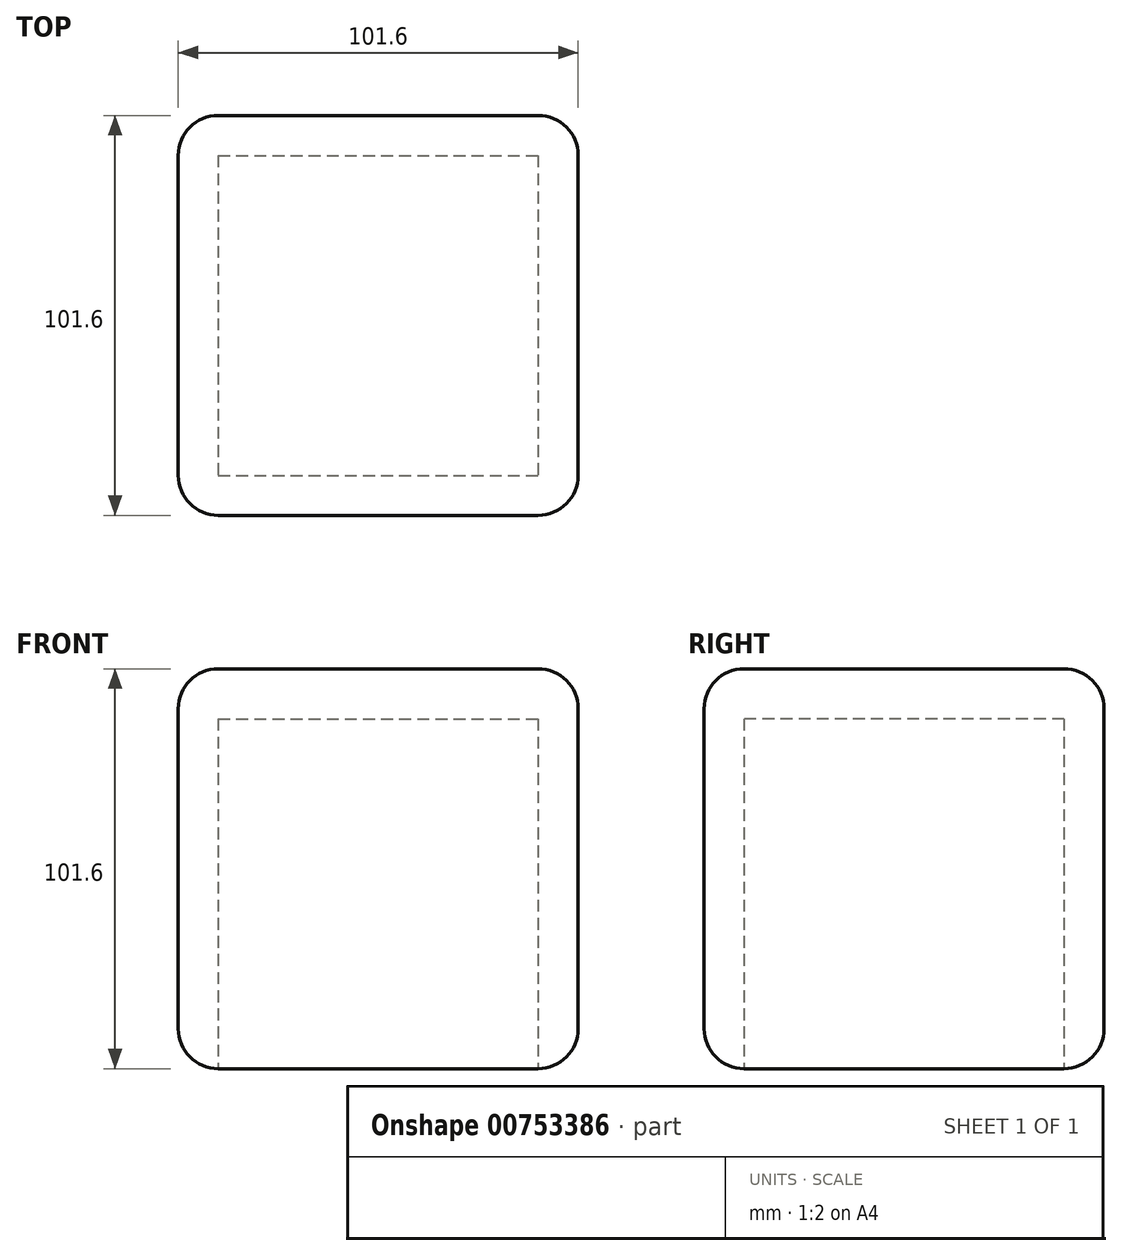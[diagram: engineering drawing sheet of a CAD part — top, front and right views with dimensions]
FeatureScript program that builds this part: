
annotation { "Feature Type Name" : "Feature", "Feature Type Description" : "" }
export const myFeature = defineFeature(function(context is Context, id is Id, definition is map)
    precondition{}
    {
        {
            var Q0;
            Q0=qCreatedBy(makeId("Top.planeOp"),FACE);
            var sketch = newSketch(context, id + "F0", { "sketchPlane" : qUnion([Q0])});
            skLineSegment(sketch, "E0.bottom", {"start": v(-50.8, 50.8) * mm, "end": v(50.8, 50.8) * mm});
            skLineSegment(sketch, "E0.top", {"start": v(-50.8, -50.8) * mm, "end": v(50.8, -50.8) * mm});
            skLineSegment(sketch, "E0.left", {"start": v(-50.8, 50.8) * mm, "end": v(-50.8, -50.8) * mm});
            skLineSegment(sketch, "E0.right", {"start": v(50.8, 50.8) * mm, "end": v(50.8, -50.8) * mm});
            skPoint(sketch, "E0.middle", {"position": v(0, 0) * mm});
            skSolve(sketch);
        }
        {
            var Q0;
            Q0=makeQuery(id+"F0.imprint","IMPRINT",FACE,{"disambiguationData":[TD([[makeQuery(id+"F0.imprint","IMPRINT",EDGE,{"derivedFrom":sQuery(id+"F0.wireOp",EDGE,"E0.bottom")}),-1.0]])]});
            extrude(context, id + "F1", {"entities" : qUnion([Q0]), "depth" : 101.6 * mm, "offsetDistance" : 25.4 * mm});
        }
        {
            var Q0;
            Q0=qCreatedBy(makeId("Top.planeOp"),FACE);
            var sketch = newSketch(context, id + "F2", { "sketchPlane" : qUnion([Q0])});
            skCircle(sketch, "E1", {"center": v(0, 0) * mm, "radius": 50.8 * mm});
            skSolve(sketch);
        }
        {
            var Q0;
            Q0=makeQuery(id+"F2.imprint","IMPRINT",FACE,{"disambiguationData":[TD([[makeQuery(id+"F2.imprint","IMPRINT",EDGE,{"derivedFrom":sQuery(id+"F2.wireOp",EDGE,"E1")}),1.0]])]});
            extrude(context, id + "F3", {"entities" : qUnion([Q0]), "depth" : 101.6 * mm, "offsetDistance" : 25.4 * mm});
        }
        {
            var Q0;
            Q0=qCreatedBy(makeId("Front.planeOp"),FACE);
            var sketch = newSketch(context, id + "F4", { "sketchPlane" : qUnion([Q0])});
            skArc(sketch, "E2", {"start": v(42.89, -27.22) * mm, "mid": v(27.22, 42.89) * mm, "end": v(-42.89, 27.22) * mm});
            skLineSegment(sketch, "E3", {"start": v(-42.89, 27.22) * mm, "end": v(42.89, -27.22) * mm});
            skSolve(sketch);
        }
        {
            var Q0;
            Q0=makeQuery(id+"F4.imprint","IMPRINT",FACE,{"disambiguationData":[TD([[makeQuery(id+"F4.imprint","IMPRINT",EDGE,{"derivedFrom":sQuery(id+"F4.wireOp",EDGE,"E2")}),1.0]])]});
            var Q1;
            Q1=sQuery(id+"F4.wireOp",EDGE,"E3");
            revolve(context, id + "F5", {"surfaceOperationType" : NewSurfaceOperationType.NEW, "entities" : qUnion([Q0]), "axis" : qUnion([Q1]), "revolveType" : RevolveType.FULL});
        }
        {
            var Q0;
            Q0=makeQuery(id+"F1.opExtrude","SWEPT_BODY",BODY,{"disambiguationData":[OSD([sQuery(id+"F0.wireOp",EDGE,"E0.bottom"),sQuery(id+"F0.wireOp",EDGE,"E0.top"),sQuery(id+"F0.wireOp",EDGE,"E0.left"),sQuery(id+"F0.wireOp",EDGE,"E0.right")])]});
            deleteBodies(context, id + "F6", {"entities" : qUnion([Q0])});
        }
        {
            var Q0;
            Q0=makeQuery(id+"F3.opExtrude","SWEPT_BODY",BODY,{"disambiguationData":[OSD([sQuery(id+"F2.wireOp",EDGE,"E1")])]});
            deleteBodies(context, id + "F7", {"entities" : qUnion([Q0])});
        }
        {
            var Q0;
            Q0=makeQuery(id+"F5.opRevolve","SWEPT_BODY",BODY,{"disambiguationData":[OSD([sQuery(id+"F4.wireOp",EDGE,"E2"),sQuery(id+"F4.wireOp",EDGE,"E3")])]});
            deleteBodies(context, id + "F8", {"entities" : qUnion([Q0])});
        }
        {
            var Q0;
            Q0=qCreatedBy(makeId("Top.planeOp"),FACE);
            var sketch = newSketch(context, id + "F9", { "sketchPlane" : qUnion([Q0])});
            skLineSegment(sketch, "E4.bottom", {"start": v(-50.8, 50.8) * mm, "end": v(50.8, 50.8) * mm});
            skLineSegment(sketch, "E4.top", {"start": v(-50.8, -50.8) * mm, "end": v(50.8, -50.8) * mm});
            skLineSegment(sketch, "E4.left", {"start": v(-50.8, 50.8) * mm, "end": v(-50.8, -50.8) * mm});
            skLineSegment(sketch, "E4.right", {"start": v(50.8, 50.8) * mm, "end": v(50.8, -50.8) * mm});
            skPoint(sketch, "E4.middle", {"position": v(0, 0) * mm});
            skSolve(sketch);
        }
        {
            var Q0;
            Q0 = qSketchRegion(id + "F9", true);
            extrude(context, id + "F10", {"entities" : qUnion([Q0]), "depth" : 101.6 * mm, "offsetDistance" : 25.4 * mm});
        }
        {
            var Q0;
            Q0=makeQuery(id+"F10.opExtrude","SWEPT_EDGE",EDGE,{"disambiguationData":[OSD([sQuery(id+"F9.wireOp",EDGE,"E4.bottom"),sQuery(id+"F9.wireOp",EDGE,"E4.left")])]});
            var Q1;
            Q1=makeQuery(id+"F10.opExtrude","CAP_EDGE",EDGE,{"disambiguationData":[OSD([sQuery(id+"F9.wireOp",EDGE,"E4.left")])],"isStart":false});
            var Q2;
            Q2=makeQuery(id+"F10.opExtrude","CAP_EDGE",EDGE,{"disambiguationData":[OSD([sQuery(id+"F9.wireOp",EDGE,"E4.bottom")])],"isStart":false});
            var Q3;
            Q3=makeQuery(id+"F10.opExtrude","CAP_EDGE",EDGE,{"disambiguationData":[OSD([sQuery(id+"F9.wireOp",EDGE,"E4.right")])],"isStart":false});
            var Q4;
            Q4=makeQuery(id+"F10.opExtrude","SWEPT_EDGE",EDGE,{"disambiguationData":[OSD([sQuery(id+"F9.wireOp",EDGE,"E4.bottom"),sQuery(id+"F9.wireOp",EDGE,"E4.right")])]});
            var Q5;
            Q5=makeQuery(id+"F10.opExtrude","SWEPT_EDGE",EDGE,{"disambiguationData":[OSD([sQuery(id+"F9.wireOp",EDGE,"E4.top"),sQuery(id+"F9.wireOp",EDGE,"E4.right")])]});
            var Q6;
            Q6=makeQuery(id+"F10.opExtrude","CAP_EDGE",EDGE,{"disambiguationData":[OSD([sQuery(id+"F9.wireOp",EDGE,"E4.right")])],"isStart":true});
            var Q7;
            Q7=makeQuery(id+"F10.opExtrude","CAP_EDGE",EDGE,{"disambiguationData":[OSD([sQuery(id+"F9.wireOp",EDGE,"E4.top")])],"isStart":true});
            var Q8;
            Q8=makeQuery(id+"F10.opExtrude","SWEPT_EDGE",EDGE,{"disambiguationData":[OSD([sQuery(id+"F9.wireOp",EDGE,"E4.top"),sQuery(id+"F9.wireOp",EDGE,"E4.left")])]});
            var Q9;
            Q9=makeQuery(id+"F10.opExtrude","CAP_EDGE",EDGE,{"disambiguationData":[OSD([sQuery(id+"F9.wireOp",EDGE,"E4.left")])],"isStart":true});
            var Q10;
            Q10=makeQuery(id+"F10.opExtrude","CAP_EDGE",EDGE,{"disambiguationData":[OSD([sQuery(id+"F9.wireOp",EDGE,"E4.bottom")])],"isStart":true});
            var Q11;
            Q11=makeQuery(id+"F10.opExtrude","CAP_EDGE",EDGE,{"disambiguationData":[OSD([sQuery(id+"F9.wireOp",EDGE,"E4.top")])],"isStart":false});
            fillet(context, id + "F11", {"entities" : qUnion([Q0, Q1, Q2, Q3, Q4, Q5, Q6, Q7, Q8, Q9, Q10, Q11]), "radius" : 10.16 * mm, "tangentPropagation" : true, "allowEdgeOverflow" : false});
        }
        {
            var Q0;
            Q0=makeQuery(id+"F10.opExtrude","CAP_FACE",FACE,{"disambiguationData":[OSD([sQuery(id+"F9.wireOp",EDGE,"E4.bottom"),sQuery(id+"F9.wireOp",EDGE,"E4.top"),sQuery(id+"F9.wireOp",EDGE,"E4.left"),sQuery(id+"F9.wireOp",EDGE,"E4.right")])],"isStart":true});
            var sketch = newSketch(context, id + "F12", { "sketchPlane" : qUnion([Q0])});
            skSolve(sketch);
        }
        {
            var Q0;
            Q0=makeQuery(id+"F10.opExtrude","CAP_FACE",FACE,{"disambiguationData":[OSD([sQuery(id+"F9.wireOp",EDGE,"E4.bottom"),sQuery(id+"F9.wireOp",EDGE,"E4.top"),sQuery(id+"F9.wireOp",EDGE,"E4.left"),sQuery(id+"F9.wireOp",EDGE,"E4.right")])],"isStart":true});
            shell(context, id + "F13", {"entities" : qUnion([Q0]), "thickness" : 12.7 * mm});
        }
        {
            var Q0;
            {var subQ0=sQuery(id+"F9.wireOp",EDGE,"E4.right");var subQ1=sQuery(id+"F9.wireOp",EDGE,"E4.left");var subQ2=sQuery(id+"F9.wireOp",EDGE,"E4.top");var subQ3=sQuery(id+"F9.wireOp",EDGE,"E4.bottom");var subQ4=makeQuery(id+"F10.opExtrude","CAP_FACE",FACE,{"disambiguationData":[OSD([subQ3,subQ2,subQ1,subQ0])],"isStart":true});Q0=makeQuery(id+"F12.imprint","IMPRINT",FACE,{"disambiguationData":[TD([[makeQuery(id+"F12.imprint","IMPRINT",EDGE,{"derivedFrom":makeQuery(id+"F11.opFillet","BLEND_EDGE",EDGE,{"blendedFrom":[makeQuery(id+"F10.opExtrude","CAP_EDGE",EDGE,{"disambiguationData":[OSD([subQ3])],"isStart":true}),subQ4],"blendedInto":[subQ4]})}),1.0]])]});}
            extrude(context, id + "F14", {"entities" : qUnion([Q0]), "operationType" : NewBodyOperationType.REMOVE, "oppositeDirection" : true, "depth" : 88.9 * mm, "offsetDistance" : 25.4 * mm});
        }
    });
